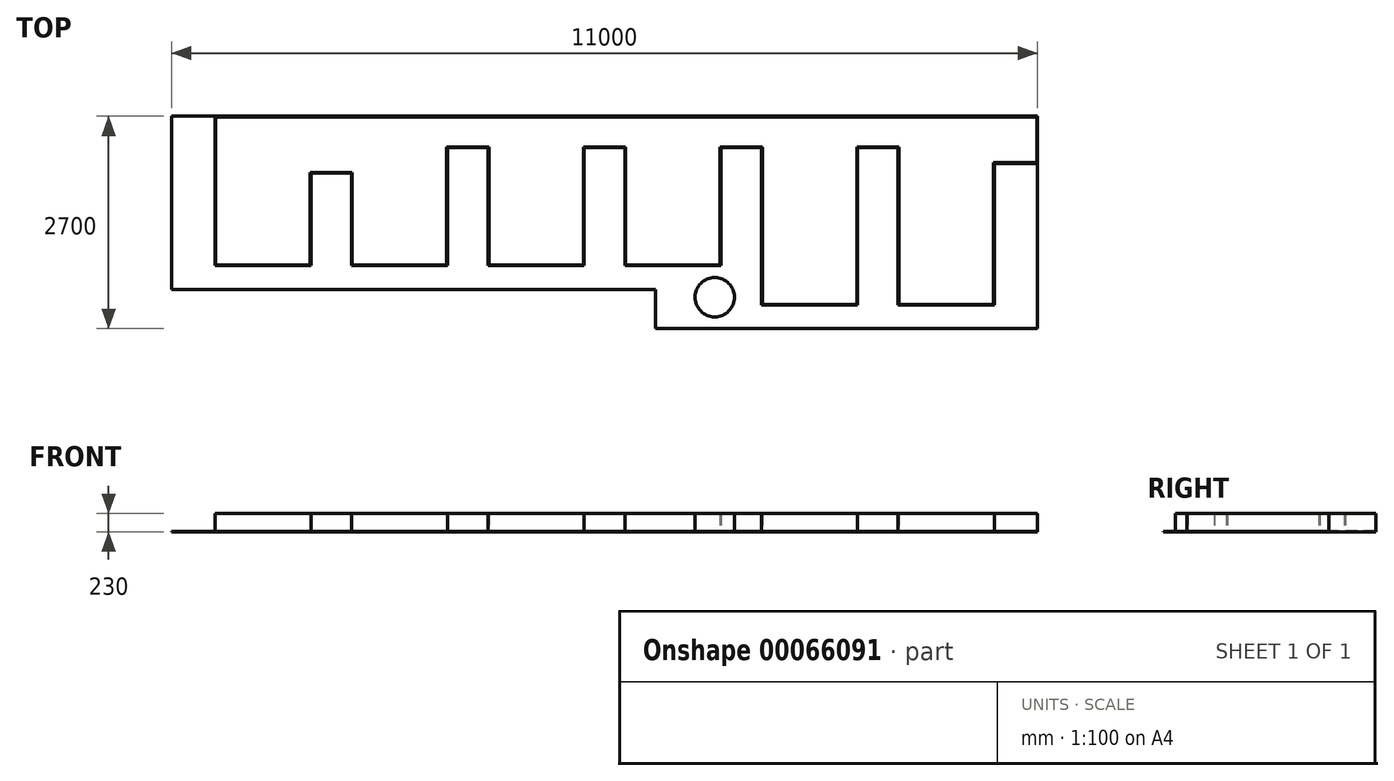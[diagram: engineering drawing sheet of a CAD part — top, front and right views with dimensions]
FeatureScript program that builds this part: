
annotation { "Feature Type Name" : "Feature", "Feature Type Description" : "" }
export const myFeature = defineFeature(function(context is Context, id is Id, definition is map)
    precondition{}
    {
        {
            var Q0;
            Q0=qCreatedBy(makeId("Top.planeOp"),FACE);
            var sketch = newSketch(context, id + "F0", { "sketchPlane" : qUnion([Q0])});
            skLineSegment(sketch, "E0", {"start": v(0, 0) * mm, "end": v(11000, 0) * mm});
            skLineSegment(sketch, "E1", {"start": v(11000, 0) * mm, "end": v(11000, -2700) * mm});
            skLineSegment(sketch, "E2", {"start": v(11000, -2700) * mm, "end": v(6150, -2700) * mm});
            skLineSegment(sketch, "E3", {"start": v(6150, -2700) * mm, "end": v(6150, -2200) * mm});
            skLineSegment(sketch, "E4", {"start": v(6150, -2200) * mm, "end": v(0, -2200) * mm});
            skLineSegment(sketch, "E5", {"start": v(0, -2200) * mm, "end": v(0, 0) * mm});
            skSolve(sketch);
        }
        {
            var Q0;
            Q0=makeQuery(id+"F0.imprint","IMPRINT",FACE,{"disambiguationData":[TD([[makeQuery(id+"F0.imprint","IMPRINT",EDGE,{"derivedFrom":sQuery(id+"F0.wireOp",EDGE,"E0")}),-1.0]])]});
            extrude(context, id + "F1", {"entities" : qUnion([Q0]), "oppositeDirection" : true, "depth" : 5 * mm});
        }
        {
            var Q0;
            Q0=makeQuery(id+"F1.opExtrude","CAP_FACE",FACE,{"disambiguationData":[OSD([sQuery(id+"F0.wireOp",EDGE,"E0"),sQuery(id+"F0.wireOp",EDGE,"E1"),sQuery(id+"F0.wireOp",EDGE,"E2"),sQuery(id+"F0.wireOp",EDGE,"E3"),sQuery(id+"F0.wireOp",EDGE,"E4"),sQuery(id+"F0.wireOp",EDGE,"E5")])],"isStart":true});
            var sketch = newSketch(context, id + "F2", { "sketchPlane" : qUnion([Q0])});
            skLineSegment(sketch, "E6.bottom", {"start": v(10300, 0) * mm, "end": v(9150, 0) * mm});
            skLineSegment(sketch, "E6.top", {"start": v(10300, -1000) * mm, "end": v(9150, -1000) * mm});
            skLineSegment(sketch, "E6.left", {"start": v(10300, 0) * mm, "end": v(10300, -1000) * mm});
            skLineSegment(sketch, "E6.right", {"start": v(9150, 0) * mm, "end": v(9150, -1000) * mm});
            skLineSegment(sketch, "E7.bottom", {"start": v(620, 0) * mm, "end": v(2870, 0) * mm});
            skLineSegment(sketch, "E7.top", {"start": v(620, -800) * mm, "end": v(2870, -800) * mm});
            skLineSegment(sketch, "E7.left", {"start": v(620, 0) * mm, "end": v(620, -800) * mm});
            skLineSegment(sketch, "E7.right", {"start": v(2870, 0) * mm, "end": v(2870, -800) * mm});
            skCircle(sketch, "E8", {"center": v(1150, -400) * mm, "radius": 260 * mm});
            skCircle(sketch, "E9", {"center": v(2250, -400) * mm, "radius": 260 * mm});
            skCircle(sketch, "E10", {"center": v(9725, -500) * mm, "radius": 320 * mm});
            skPoint(sketch, "E10.centerSnap0", {"position": v(9150, -500) * mm});
            skPoint(sketch, "E11", {"position": v(9725, -1000) * mm});
            skPoint(sketch, "E12", {"position": v(620, -400) * mm});
            skSolve(sketch);
        }
        {
            var Q0;
            Q0=makeQuery(id+"F2.imprint","IMPRINT",FACE,{"disambiguationData":[TD([[makeQuery(id+"F2.imprint","IMPRINT",EDGE,{"derivedFrom":sQuery(id+"F2.wireOp",EDGE,"E8")}),1.0]])]});
            var Q1;
            Q1=makeQuery(id+"F2.imprint","IMPRINT",FACE,{"disambiguationData":[TD([[makeQuery(id+"F2.imprint","IMPRINT",EDGE,{"derivedFrom":sQuery(id+"F2.wireOp",EDGE,"E9")}),1.0]])]});
            var Q2;
            Q2=makeQuery(id+"F2.imprint","IMPRINT",FACE,{"disambiguationData":[TD([[makeQuery(id+"F2.imprint","IMPRINT",EDGE,{"derivedFrom":sQuery(id+"F2.wireOp",EDGE,"E10")}),1.0]])]});
            extrude(context, id + "F3", {"entities" : qUnion([Q0, Q1, Q2]), "depth" : 200 * mm});
        }
        {
            var Q0;
            Q0=makeQuery(id+"F1.opExtrude","CAP_FACE",FACE,{"disambiguationData":[OSD([sQuery(id+"F0.wireOp",EDGE,"E0"),sQuery(id+"F0.wireOp",EDGE,"E1"),sQuery(id+"F0.wireOp",EDGE,"E2"),sQuery(id+"F0.wireOp",EDGE,"E3"),sQuery(id+"F0.wireOp",EDGE,"E4"),sQuery(id+"F0.wireOp",EDGE,"E5")])],"isStart":true});
            var sketch = newSketch(context, id + "F4", { "sketchPlane" : qUnion([Q0])});
            skLineSegment(sketch, "E13", {"start": v(550, 0) * mm, "end": v(550, -1900) * mm});
            skLineSegment(sketch, "E14", {"start": v(550, -1900) * mm, "end": v(1770, -1900) * mm});
            skLineSegment(sketch, "E15", {"start": v(1770, -1900) * mm, "end": v(1770, -725) * mm});
            skLineSegment(sketch, "E16", {"start": v(1770, -725) * mm, "end": v(2286, -725) * mm});
            skLineSegment(sketch, "E17", {"start": v(2286, -725) * mm, "end": v(2286, -1900) * mm});
            skLineSegment(sketch, "E18", {"start": v(2286, -1900) * mm, "end": v(3506, -1900) * mm});
            skLineSegment(sketch, "E19", {"start": v(3506, -1900) * mm, "end": v(3506, -400) * mm});
            skLineSegment(sketch, "E20", {"start": v(3506, -400) * mm, "end": v(4022, -400) * mm});
            skLineSegment(sketch, "E21", {"start": v(4022, -400) * mm, "end": v(4022, -1900) * mm});
            skLineSegment(sketch, "E22", {"start": v(4022, -1900) * mm, "end": v(5242, -1900) * mm});
            skLineSegment(sketch, "E23", {"start": v(5242, -1900) * mm, "end": v(5242, -400) * mm});
            skLineSegment(sketch, "E24", {"start": v(5242, -400) * mm, "end": v(5758, -400) * mm});
            skLineSegment(sketch, "E25", {"start": v(5758, -400) * mm, "end": v(5758, -1900) * mm});
            skLineSegment(sketch, "E26", {"start": v(6978, -1900) * mm, "end": v(6978, -400) * mm});
            skLineSegment(sketch, "E27", {"start": v(6978, -400) * mm, "end": v(7494, -400) * mm});
            skLineSegment(sketch, "E28", {"start": v(7494, -400) * mm, "end": v(7494, -2400) * mm});
            skLineSegment(sketch, "E29", {"start": v(7494, -2400) * mm, "end": v(8714, -2400) * mm});
            skLineSegment(sketch, "E30", {"start": v(8714, -2400) * mm, "end": v(8714, -400) * mm});
            skLineSegment(sketch, "E31", {"start": v(8714, -400) * mm, "end": v(9230, -400) * mm});
            skLineSegment(sketch, "E32", {"start": v(9230, -400) * mm, "end": v(9230, -2400) * mm});
            skLineSegment(sketch, "E33", {"start": v(9230, -2400) * mm, "end": v(10450, -2400) * mm});
            skLineSegment(sketch, "E34", {"start": v(10450, -2400) * mm, "end": v(10450, -600) * mm});
            skLineSegment(sketch, "E35", {"start": v(10450, -600) * mm, "end": v(11000, -600) * mm});
            skLineSegment(sketch, "E36", {"start": v(11000, -600) * mm, "end": v(11000, 0) * mm});
            skLineSegment(sketch, "E37", {"start": v(11000, 0) * mm, "end": v(550, 0) * mm});
            skLineSegment(sketch, "E38", {"start": v(5758, -1900) * mm, "end": v(6978, -1900) * mm});
            skCircle(sketch, "E39", {"center": v(6900, -2300) * mm, "radius": 250 * mm});
            skSolve(sketch);
        }
        {
            var Q0;
            Q0=makeQuery(id+"F4.imprint","IMPRINT",FACE,{"disambiguationData":[TD([[makeQuery(id+"F4.imprint","IMPRINT",EDGE,{"derivedFrom":sQuery(id+"F4.wireOp",EDGE,"E13")}),1.0]])]});
            var Q1;
            Q1=makeQuery(id+"F4.imprint","IMPRINT",FACE,{"disambiguationData":[TD([[makeQuery(id+"F4.imprint","IMPRINT",EDGE,{"derivedFrom":sQuery(id+"F4.wireOp",EDGE,"E39")}),1.0]])]});
            extrude(context, id + "F5", {"entities" : qUnion([Q0, Q1]), "operationType" : NewBodyOperationType.ADD, "depth" : 225 * mm});
        }
        {
            var Q0;
            Q0=makeQuery(id+"F5.opExtrude","CAP_FACE",FACE,{"disambiguationData":[OSD([sQuery(id+"F4.wireOp",EDGE,"E13"),sQuery(id+"F4.wireOp",EDGE,"E14"),sQuery(id+"F4.wireOp",EDGE,"E15"),sQuery(id+"F4.wireOp",EDGE,"E16"),sQuery(id+"F4.wireOp",EDGE,"E17"),sQuery(id+"F4.wireOp",EDGE,"E18"),sQuery(id+"F4.wireOp",EDGE,"E19"),sQuery(id+"F4.wireOp",EDGE,"E20"),sQuery(id+"F4.wireOp",EDGE,"E21"),sQuery(id+"F4.wireOp",EDGE,"E22"),sQuery(id+"F4.wireOp",EDGE,"E23"),sQuery(id+"F4.wireOp",EDGE,"E24"),sQuery(id+"F4.wireOp",EDGE,"E25"),sQuery(id+"F4.wireOp",EDGE,"1zntnhsd-rG3i-NkLb-fIsL-XX26f9r4blzO"),sQuery(id+"F4.wireOp",EDGE,"E26"),sQuery(id+"F4.wireOp",EDGE,"E27"),sQuery(id+"F4.wireOp",EDGE,"E28"),sQuery(id+"F4.wireOp",EDGE,"E29"),sQuery(id+"F4.wireOp",EDGE,"E30"),sQuery(id+"F4.wireOp",EDGE,"E31"),sQuery(id+"F4.wireOp",EDGE,"E32"),sQuery(id+"F4.wireOp",EDGE,"E33"),sQuery(id+"F4.wireOp",EDGE,"E34"),sQuery(id+"F4.wireOp",EDGE,"E35"),sQuery(id+"F4.wireOp",EDGE,"E36"),sQuery(id+"F4.wireOp",EDGE,"E37"),sQuery(id+"F4.wireOp",EDGE,"m1UwcAEC-0e3m-UmN5-7GTt-NpMtPrNK4Brc"),sQuery(id+"F4.wireOp",EDGE,"BkWF0MFz-75eD-Zqlv-rRHf-TpMoDsHC7V7D"),sQuery(id+"F4.wireOp",EDGE,"E38"),sQuery(id+"F4.wireOp",EDGE,"t4y7gwZb-G8Q8-nA6A-5qXL-STbEjG2zf6vN")])],"isStart":false});
            var Q1;
            Q1=makeQuery(id+"F5.opExtrude","CAP_FACE",FACE,{"disambiguationData":[OSD([sQuery(id+"F4.wireOp",EDGE,"E39")])],"isStart":false});
            shell(context, id + "F6", {"entities" : qUnion([Q0, Q1]), "thickness" : 10 * mm});
        }
    });
